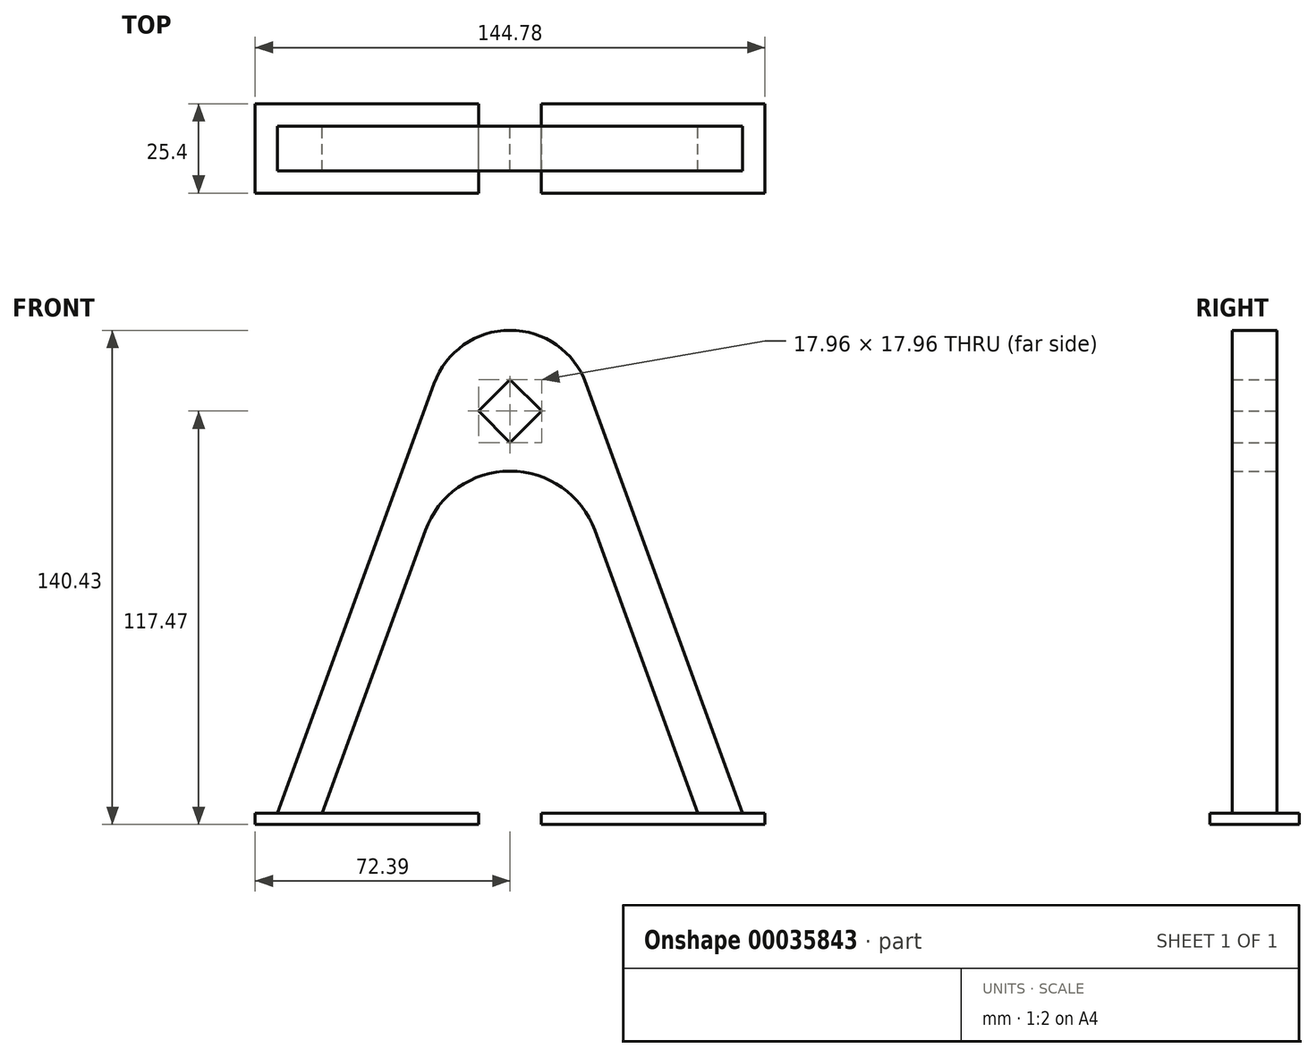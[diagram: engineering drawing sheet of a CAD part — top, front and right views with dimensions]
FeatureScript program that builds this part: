
annotation { "Feature Type Name" : "Feature", "Feature Type Description" : "" }
export const myFeature = defineFeature(function(context is Context, id is Id, definition is map)
    precondition{}
    {
        {
            var Q0;
            Q0=qCreatedBy(makeId("Front.planeOp"),FACE);
            var sketch = newSketch(context, id + "F0", { "sketchPlane" : qUnion([Q0])});
            skLineSegment(sketch, "E0", {"start": v(-21.6, 7.83) * mm, "end": v(-66.04, -114.3) * mm});
            skLineSegment(sketch, "E1", {"start": v(-66.04, -114.3) * mm, "end": v(-53.34, -114.3) * mm});
            skLineSegment(sketch, "E2", {"start": v(-53.34, -114.3) * mm, "end": v(-24.08, -33.92) * mm});
            skLineSegment(sketch, "E3", {"start": v(24.08, -33.92) * mm, "end": v(53.34, -114.3) * mm});
            skLineSegment(sketch, "E4", {"start": v(53.34, -114.3) * mm, "end": v(66.04, -114.3) * mm});
            skLineSegment(sketch, "E5", {"start": v(66.04, -114.3) * mm, "end": v(21.59, 7.83) * mm});
            skLineSegment(sketch, "E6", {"start": v(0, 167.93) * mm, "end": v(0, 0) * mm, "construction": true});
            skArc(sketch, "E7.trimOffspring", {"start": v(21.59, 7.83) * mm, "mid": v(0, 22.96) * mm, "end": v(-21.6, 7.83) * mm});
            skLineSegment(sketch, "E8.rect.bottom", {"start": v(8.98, 0) * mm, "end": v(0, -8.98) * mm});
            skLineSegment(sketch, "E8.rect.top", {"start": v(0, 8.98) * mm, "end": v(-8.98, 0) * mm});
            skLineSegment(sketch, "E8.rect.left", {"start": v(8.98, 0) * mm, "end": v(0, 8.98) * mm});
            skLineSegment(sketch, "E8.rect.right", {"start": v(0, -8.98) * mm, "end": v(-8.98, 0) * mm});
            skLineSegment(sketch, "E9", {"start": v(-0.05, -17.05) * mm, "end": v(-0.05, -17.05) * mm});
            skArc(sketch, "E10.filletArc", {"start": v(-0.05, -17.05) * mm, "mid": v(-14.72, -21.7) * mm, "end": v(-24.08, -33.92) * mm});
            skArc(sketch, "E11.filletArc", {"start": v(24.08, -33.92) * mm, "mid": v(14.68, -21.67) * mm, "end": v(-0.05, -17.05) * mm});
            skSolve(sketch);
        }
        {
            var Q0;
            Q0=makeQuery(id+"F0.imprint","IMPRINT",FACE,{"disambiguationData":[TD([[makeQuery(id+"F0.imprint","IMPRINT",EDGE,{"derivedFrom":sQuery(id+"F0.wireOp",EDGE,"E0")}),1.0]])]});
            extrude(context, id + "F1", {"entities" : qUnion([Q0]), "depth" : 12.7 * mm});
        }
        {
            var Q0;
            Q0=makeQuery(id+"F1.opExtrude","SWEPT_FACE",FACE,{"disambiguationData":[OSD([sQuery(id+"F0.wireOp",EDGE,"E1")])]});
            var sketch = newSketch(context, id + "F2", { "sketchPlane" : qUnion([Q0])});
            skLineSegment(sketch, "E12.bottom", {"start": v(-72.39, 19.05) * mm, "end": v(-8.89, 19.05) * mm});
            skLineSegment(sketch, "E12.top", {"start": v(-72.39, -6.35) * mm, "end": v(-8.89, -6.35) * mm});
            skLineSegment(sketch, "E12.left", {"start": v(-72.39, 19.05) * mm, "end": v(-72.39, -6.35) * mm});
            skLineSegment(sketch, "E12.right", {"start": v(-8.89, 19.05) * mm, "end": v(-8.89, -6.35) * mm});
            skSolve(sketch);
        }
        {
            var Q0;
            Q0 = qSketchRegion(id + "F2", true);
            extrude(context, id + "F3", {"entities" : qUnion([Q0]), "operationType" : NewBodyOperationType.ADD, "depth" : 3.17 * mm});
        }
        {
            var Q0;
            Q0=makeQuery(id+"F1.opExtrude","SWEPT_FACE",FACE,{"disambiguationData":[OSD([sQuery(id+"F0.wireOp",EDGE,"E4")])]});
            var sketch = newSketch(context, id + "F4", { "sketchPlane" : qUnion([Q0])});
            skLineSegment(sketch, "E13.bottom", {"start": v(8.9, 19.05) * mm, "end": v(72.4, 19.05) * mm});
            skLineSegment(sketch, "E13.top", {"start": v(8.9, -6.35) * mm, "end": v(72.4, -6.35) * mm});
            skLineSegment(sketch, "E13.left", {"start": v(8.9, 19.05) * mm, "end": v(8.9, -6.35) * mm});
            skLineSegment(sketch, "E13.right", {"start": v(72.4, 19.05) * mm, "end": v(72.4, -6.35) * mm});
            skSolve(sketch);
        }
        {
            var Q0;
            Q0 = qSketchRegion(id + "F4", true);
            extrude(context, id + "F5", {"entities" : qUnion([Q0]), "operationType" : NewBodyOperationType.ADD, "depth" : 3.17 * mm});
        }
    });
